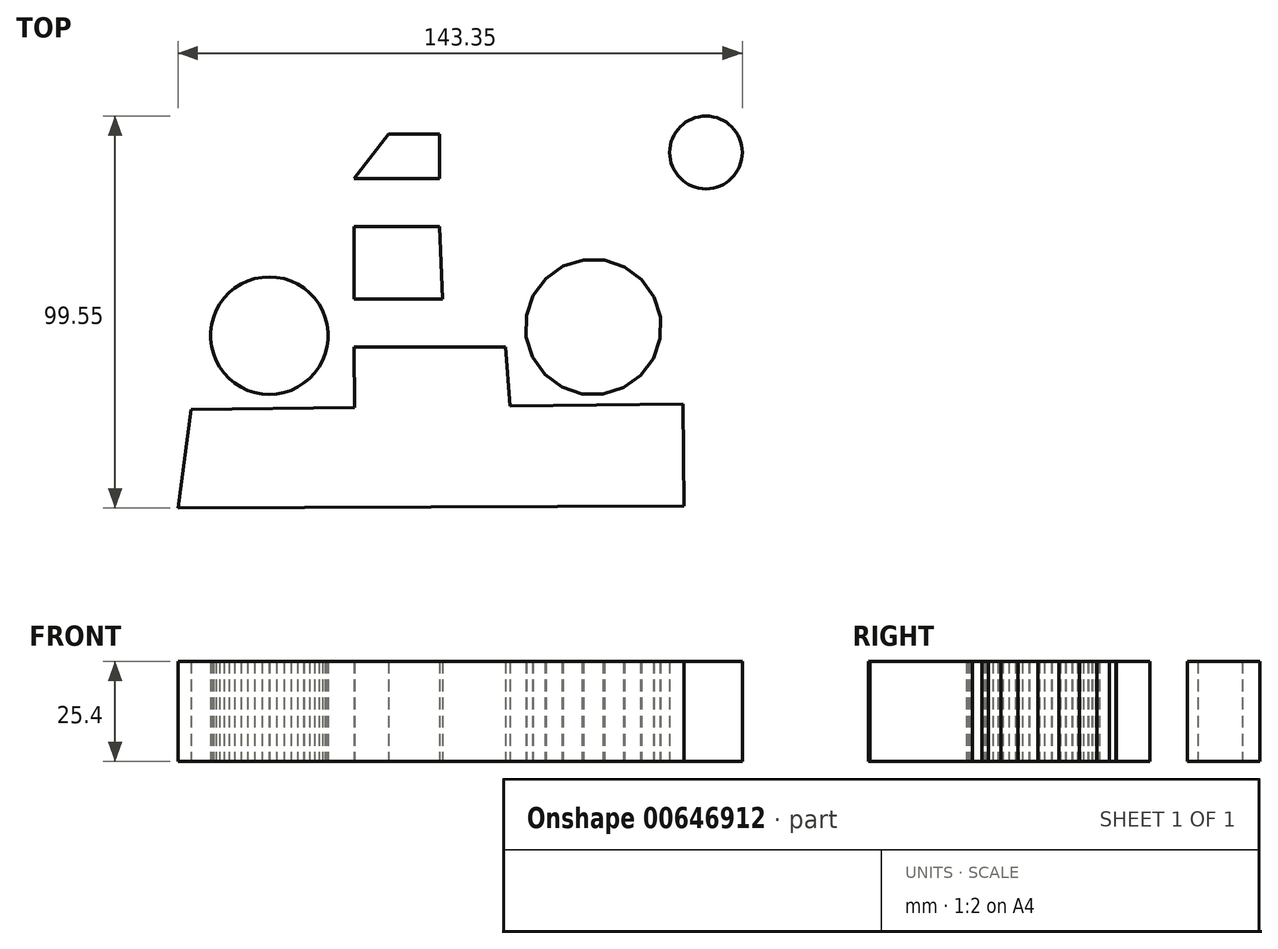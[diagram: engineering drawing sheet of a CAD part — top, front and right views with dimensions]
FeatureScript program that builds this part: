
annotation { "Feature Type Name" : "Feature", "Feature Type Description" : "" }
export const myFeature = defineFeature(function(context is Context, id is Id, definition is map)
    precondition{}
    {
        {
            var Q0;
            Q0=qCreatedBy(makeId("Top.planeOp"),FACE);
            var sketch = newSketch(context, id + "F0", { "sketchPlane" : qUnion([Q0])});
            skCircle(sketch, "E0.cCircle", {"center": v(-44.06, -3.83) * mm, "radius": 14.9 * mm, "construction": true});
            skLineSegment(sketch, "E0.0", {"start": v(-33.85, -14.73) * mm, "end": v(-35.3, -15.92) * mm});
            skLineSegment(sketch, "E0.1", {"start": v(-35.3, -15.92) * mm, "end": v(-36.88, -16.93) * mm});
            skLineSegment(sketch, "E0.2", {"start": v(-36.88, -16.93) * mm, "end": v(-38.58, -17.72) * mm});
            skLineSegment(sketch, "E0.3", {"start": v(-38.58, -17.72) * mm, "end": v(-40.37, -18.3) * mm});
            skLineSegment(sketch, "E0.4", {"start": v(-40.37, -18.3) * mm, "end": v(-42.2, -18.65) * mm});
            skLineSegment(sketch, "E0.5", {"start": v(-42.2, -18.65) * mm, "end": v(-44.08, -18.77) * mm});
            skLineSegment(sketch, "E0.6", {"start": v(-44.08, -18.77) * mm, "end": v(-45.95, -18.65) * mm});
            skLineSegment(sketch, "E0.7", {"start": v(-45.95, -18.65) * mm, "end": v(-47.8, -18.3) * mm});
            skLineSegment(sketch, "E0.8", {"start": v(-47.8, -18.3) * mm, "end": v(-49.58, -17.71) * mm});
            skLineSegment(sketch, "E0.9", {"start": v(-49.58, -17.71) * mm, "end": v(-51.27, -16.91) * mm});
            skLineSegment(sketch, "E0.10", {"start": v(-51.27, -16.91) * mm, "end": v(-52.86, -15.9) * mm});
            skLineSegment(sketch, "E0.11", {"start": v(-52.86, -15.9) * mm, "end": v(-54.3, -14.7) * mm});
            skLineSegment(sketch, "E0.12", {"start": v(-54.3, -14.7) * mm, "end": v(-55.58, -13.34) * mm});
            skLineSegment(sketch, "E0.13", {"start": v(-55.58, -13.34) * mm, "end": v(-56.68, -11.82) * mm});
            skLineSegment(sketch, "E0.14", {"start": v(-56.68, -11.82) * mm, "end": v(-57.59, -10.18) * mm});
            skLineSegment(sketch, "E0.15", {"start": v(-57.59, -10.18) * mm, "end": v(-58.27, -8.43) * mm});
            skLineSegment(sketch, "E0.16", {"start": v(-58.27, -8.43) * mm, "end": v(-58.74, -6.61) * mm});
            skLineSegment(sketch, "E0.17", {"start": v(-58.74, -6.61) * mm, "end": v(-58.97, -4.75) * mm});
            skLineSegment(sketch, "E0.18", {"start": v(-58.97, -4.75) * mm, "end": v(-58.97, -2.88) * mm});
            skLineSegment(sketch, "E0.19", {"start": v(-58.97, -2.88) * mm, "end": v(-58.73, -1.02) * mm});
            skLineSegment(sketch, "E0.20", {"start": v(-58.73, -1.02) * mm, "end": v(-58.26, 0.8) * mm});
            skLineSegment(sketch, "E0.21", {"start": v(-58.26, 0.8) * mm, "end": v(-57.57, 2.54) * mm});
            skLineSegment(sketch, "E0.22", {"start": v(-57.57, 2.54) * mm, "end": v(-56.67, 4.18) * mm});
            skLineSegment(sketch, "E0.23", {"start": v(-56.67, 4.18) * mm, "end": v(-55.56, 5.7) * mm});
            skLineSegment(sketch, "E0.24", {"start": v(-55.56, 5.7) * mm, "end": v(-54.28, 7.07) * mm});
            skLineSegment(sketch, "E0.25", {"start": v(-54.28, 7.07) * mm, "end": v(-52.83, 8.26) * mm});
            skLineSegment(sketch, "E0.26", {"start": v(-52.83, 8.26) * mm, "end": v(-51.25, 9.26) * mm});
            skLineSegment(sketch, "E0.27", {"start": v(-51.25, 9.26) * mm, "end": v(-49.55, 10.06) * mm});
            skLineSegment(sketch, "E0.28", {"start": v(-49.55, 10.06) * mm, "end": v(-47.76, 10.64) * mm});
            skLineSegment(sketch, "E0.29", {"start": v(-47.76, 10.64) * mm, "end": v(-45.92, 10.99) * mm});
            skLineSegment(sketch, "E0.30", {"start": v(-45.92, 10.99) * mm, "end": v(-44.05, 11.1) * mm});
            skLineSegment(sketch, "E0.31", {"start": v(-44.05, 11.1) * mm, "end": v(-42.18, 10.98) * mm});
            skLineSegment(sketch, "E0.32", {"start": v(-42.18, 10.98) * mm, "end": v(-40.33, 10.63) * mm});
            skLineSegment(sketch, "E0.33", {"start": v(-40.33, 10.63) * mm, "end": v(-38.55, 10.05) * mm});
            skLineSegment(sketch, "E0.34", {"start": v(-38.55, 10.05) * mm, "end": v(-36.86, 9.25) * mm});
            skLineSegment(sketch, "E0.35", {"start": v(-36.86, 9.25) * mm, "end": v(-35.27, 8.24) * mm});
            skLineSegment(sketch, "E0.36", {"start": v(-35.27, 8.24) * mm, "end": v(-33.83, 7.04) * mm});
            skLineSegment(sketch, "E0.37", {"start": v(-33.83, 7.04) * mm, "end": v(-32.55, 5.68) * mm});
            skLineSegment(sketch, "E0.38", {"start": v(-32.55, 5.68) * mm, "end": v(-31.45, 4.16) * mm});
            skLineSegment(sketch, "E0.39", {"start": v(-31.45, 4.16) * mm, "end": v(-30.54, 2.51) * mm});
            skLineSegment(sketch, "E0.40", {"start": v(-30.54, 2.51) * mm, "end": v(-29.86, 0.77) * mm});
            skLineSegment(sketch, "E0.41", {"start": v(-29.86, 0.77) * mm, "end": v(-29.4, -1.05) * mm});
            skLineSegment(sketch, "E0.42", {"start": v(-29.4, -1.05) * mm, "end": v(-29.16, -2.91) * mm});
            skLineSegment(sketch, "E0.43", {"start": v(-29.16, -2.91) * mm, "end": v(-29.16, -4.79) * mm});
            skLineSegment(sketch, "E0.44", {"start": v(-29.16, -4.79) * mm, "end": v(-29.4, -6.65) * mm});
            skLineSegment(sketch, "E0.45", {"start": v(-29.4, -6.65) * mm, "end": v(-29.87, -8.46) * mm});
            skLineSegment(sketch, "E0.46", {"start": v(-29.87, -8.46) * mm, "end": v(-30.56, -10.2) * mm});
            skLineSegment(sketch, "E0.47", {"start": v(-30.56, -10.2) * mm, "end": v(-31.46, -11.85) * mm});
            skLineSegment(sketch, "E0.48", {"start": v(-31.46, -11.85) * mm, "end": v(-32.57, -13.36) * mm});
            skLineSegment(sketch, "E0.49", {"start": v(-32.57, -13.36) * mm, "end": v(-33.85, -14.73) * mm});
            skPoint(sketch, "E0.0.midPoint", {"position": v(-34.58, -15.33) * mm});
            skCircle(sketch, "E1.cCircle", {"center": v(38.23, -1.64) * mm, "radius": 17.01 * mm, "construction": true});
            skLineSegment(sketch, "E1.0", {"start": v(50.28, -13.95) * mm, "end": v(45.88, -17.07) * mm});
            skLineSegment(sketch, "E1.1", {"start": v(45.88, -17.07) * mm, "end": v(40.74, -18.68) * mm});
            skLineSegment(sketch, "E1.2", {"start": v(40.74, -18.68) * mm, "end": v(35.35, -18.62) * mm});
            skLineSegment(sketch, "E1.3", {"start": v(35.35, -18.62) * mm, "end": v(30.25, -16.9) * mm});
            skLineSegment(sketch, "E1.4", {"start": v(30.25, -16.9) * mm, "end": v(25.92, -13.7) * mm});
            skLineSegment(sketch, "E1.5", {"start": v(25.92, -13.7) * mm, "end": v(22.8, -9.3) * mm});
            skLineSegment(sketch, "E1.6", {"start": v(22.8, -9.3) * mm, "end": v(21.19, -4.16) * mm});
            skLineSegment(sketch, "E1.7", {"start": v(21.19, -4.16) * mm, "end": v(21.24, 1.23) * mm});
            skLineSegment(sketch, "E1.8", {"start": v(21.24, 1.23) * mm, "end": v(22.96, 6.34) * mm});
            skLineSegment(sketch, "E1.9", {"start": v(22.96, 6.34) * mm, "end": v(26.18, 10.66) * mm});
            skLineSegment(sketch, "E1.10", {"start": v(26.18, 10.66) * mm, "end": v(30.57, 13.79) * mm});
            skLineSegment(sketch, "E1.11", {"start": v(30.57, 13.79) * mm, "end": v(35.71, 15.4) * mm});
            skLineSegment(sketch, "E1.12", {"start": v(35.71, 15.4) * mm, "end": v(41.1, 15.34) * mm});
            skLineSegment(sketch, "E1.13", {"start": v(41.1, 15.34) * mm, "end": v(46.2, 13.62) * mm});
            skLineSegment(sketch, "E1.14", {"start": v(46.2, 13.62) * mm, "end": v(50.53, 10.4) * mm});
            skLineSegment(sketch, "E1.15", {"start": v(50.53, 10.4) * mm, "end": v(53.65, 6.01) * mm});
            skLineSegment(sketch, "E1.16", {"start": v(53.65, 6.01) * mm, "end": v(55.26, 0.87) * mm});
            skLineSegment(sketch, "E1.17", {"start": v(55.26, 0.87) * mm, "end": v(55.2, -4.52) * mm});
            skLineSegment(sketch, "E1.18", {"start": v(55.2, -4.52) * mm, "end": v(53.49, -9.62) * mm});
            skLineSegment(sketch, "E1.19", {"start": v(53.49, -9.62) * mm, "end": v(50.28, -13.95) * mm});
            skPoint(sketch, "E1.0.midPoint", {"position": v(48.08, -15.5) * mm});
            skSolve(sketch);
        }
        {
            var Q0;
            Q0=makeQuery(id+"F0.imprint","IMPRINT",FACE,{"disambiguationData":[TD([[makeQuery(id+"F0.imprint","IMPRINT",EDGE,{"derivedFrom":sQuery(id+"F0.wireOp",EDGE,"E0.0")}),-1.0]])]});
            var Q1;
            Q1=makeQuery(id+"F0.imprint","IMPRINT",FACE,{"disambiguationData":[TD([[makeQuery(id+"F0.imprint","IMPRINT",EDGE,{"derivedFrom":sQuery(id+"F0.wireOp",EDGE,"E1.0")}),-1.0]])]});
            extrude(context, id + "F1", {"entities" : qUnion([Q0, Q1]), "depth" : 25.4 * mm, "offsetDistance" : 25.4 * mm});
        }
        {
            var Q0;
            Q0=qCreatedBy(makeId("Top.planeOp"),FACE);
            var sketch = newSketch(context, id + "F2", { "sketchPlane" : qUnion([Q0])});
            skLineSegment(sketch, "E2", {"start": v(-35.67, 32.3) * mm, "end": v(-55.2, 32.3) * mm});
            skLineSegment(sketch, "E3", {"start": v(-55.2, 32.3) * mm, "end": v(-55.2, 18.06) * mm});
            skLineSegment(sketch, "E4", {"start": v(-55.2, 18.06) * mm, "end": v(-44.06, 18.06) * mm});
            skLineSegment(sketch, "E5", {"start": v(-44.06, 18.06) * mm, "end": v(-33.48, 6.75) * mm});
            skLineSegment(sketch, "E6", {"start": v(-35.67, 32.3) * mm, "end": v(-22.53, 52.55) * mm});
            skLineSegment(sketch, "E7", {"start": v(-22.53, 52.55) * mm, "end": v(57.75, 52.55) * mm});
            skLineSegment(sketch, "E8", {"start": v(57.75, 52.55) * mm, "end": v(57.75, 23.9) * mm});
            skLineSegment(sketch, "E9", {"start": v(57.75, 23.9) * mm, "end": v(29.29, 13.32) * mm});
            skLineSegment(sketch, "E10", {"start": v(-28.56, -4.38) * mm, "end": v(20.9, -4.38) * mm});
            skLineSegment(sketch, "E11", {"start": v(21.62, 3.47) * mm, "end": v(-29.83, 1.46) * mm});
            skLineSegment(sketch, "E12", {"start": v(-22.53, 36.13) * mm, "end": v(-0.82, 36.13) * mm});
            skLineSegment(sketch, "E13", {"start": v(-0.82, 36.13) * mm, "end": v(-0.82, 47.44) * mm});
            skLineSegment(sketch, "E14", {"start": v(-0.82, 47.44) * mm, "end": v(-13.78, 47.44) * mm});
            skLineSegment(sketch, "E15", {"start": v(-13.78, 47.44) * mm, "end": v(-22.53, 36.13) * mm});
            skLineSegment(sketch, "E16", {"start": v(-22.53, 23.9) * mm, "end": v(-0.82, 23.9) * mm});
            skLineSegment(sketch, "E17", {"start": v(-0.82, 23.9) * mm, "end": v(-0.1, 5.49) * mm});
            skLineSegment(sketch, "E18", {"start": v(-0.1, 5.49) * mm, "end": v(-22.53, 5.49) * mm});
            skLineSegment(sketch, "E19", {"start": v(-22.53, 5.49) * mm, "end": v(-22.53, 23.9) * mm});
            skSolve(sketch);
        }
        {
            var Q0;
            Q0=qCreatedBy(makeId("Top.planeOp"),FACE);
            var sketch = newSketch(context, id + "F3", { "sketchPlane" : qUnion([Q0])});
            skCircle(sketch, "E20", {"center": v(66.87, 42.7) * mm, "radius": 9.24 * mm});
            skSolve(sketch);
        }
        {
            var Q0;
            Q0=makeQuery(id+"F3.imprint","IMPRINT",FACE,{"disambiguationData":[TD([[makeQuery(id+"F3.imprint","IMPRINT",EDGE,{"derivedFrom":sQuery(id+"F3.wireOp",EDGE,"E20")}),1.0]])]});
            var Q1;
            Q1=makeQuery(id+"F2.imprint","IMPRINT",FACE,{"disambiguationData":[TD([[makeQuery(id+"F2.imprint","IMPRINT",EDGE,{"derivedFrom":sQuery(id+"F2.wireOp",EDGE,"E12")}),1.0]])]});
            var Q2;
            Q2=makeQuery(id+"F2.imprint","IMPRINT",FACE,{"disambiguationData":[TD([[makeQuery(id+"F2.imprint","IMPRINT",EDGE,{"derivedFrom":sQuery(id+"F2.wireOp",EDGE,"E16")}),-1.0]])]});
            extrude(context, id + "F4", {"entities" : qUnion([Q0, Q1, Q2]), "depth" : 25.4 * mm, "offsetDistance" : 25.4 * mm});
        }
        {
            var Q0;
            Q0=qCreatedBy(makeId("Top.planeOp"),FACE);
            var sketch = newSketch(context, id + "F5", { "sketchPlane" : qUnion([Q0])});
            skLineSegment(sketch, "E21", {"start": v(-50.45, 19.89) * mm, "end": v(-33.3, 7.12) * mm});
            skLineSegment(sketch, "E22", {"start": v(-50.45, 19.89) * mm, "end": v(-50.45, 31.57) * mm});
            skLineSegment(sketch, "E23", {"start": v(-50.27, 31.57) * mm, "end": v(-40.05, 31.57) * mm});
            skLineSegment(sketch, "E24", {"start": v(-40.05, 31.57) * mm, "end": v(-17.06, 62.45) * mm});
            skLineSegment(sketch, "E25", {"start": v(-17.06, 62.45) * mm, "end": v(55.92, 62.45) * mm});
            skLineSegment(sketch, "E26", {"start": v(55.92, 62.45) * mm, "end": v(53.92, 7.12) * mm});
            skLineSegment(sketch, "E27", {"start": v(-30.02, -6.75) * mm, "end": v(21.26, -6.75) * mm});
            skLineSegment(sketch, "E28", {"start": v(21.07, 1.46) * mm, "end": v(-29.65, 1.46) * mm});
            skLineSegment(sketch, "E29", {"start": v(40.6, 46.16) * mm, "end": v(25.09, 45.98) * mm});
            skLineSegment(sketch, "E30", {"start": v(25.09, 45.98) * mm, "end": v(25.22, 34.68) * mm});
            skLineSegment(sketch, "E31", {"start": v(25.22, 34.68) * mm, "end": v(41.51, 34.87) * mm});
            skLineSegment(sketch, "E32", {"start": v(41.51, 35.22) * mm, "end": v(40.6, 46.35) * mm});
            skLineSegment(sketch, "E33", {"start": v(27.46, 34.7) * mm, "end": v(27.63, 19.89) * mm});
            skLineSegment(sketch, "E34", {"start": v(41.51, 34.87) * mm, "end": v(27.63, 19.89) * mm});
            skLineSegment(sketch, "E35", {"start": v(27.63, 19.89) * mm, "end": v(-0.46, 5.66) * mm});
            skLineSegment(sketch, "E36", {"start": v(25.09, 45.98) * mm, "end": v(-0.46, 37.22) * mm});
            skLineSegment(sketch, "E37", {"start": v(-16.88, 62.77) * mm, "end": v(-17.06, 67.88) * mm});
            skLineSegment(sketch, "E38", {"start": v(-17.06, 67.88) * mm, "end": v(56.29, 67.88) * mm});
            skLineSegment(sketch, "E39", {"start": v(56.29, 67.88) * mm, "end": v(55.92, 62.77) * mm});
            skLineSegment(sketch, "E40", {"start": v(56.29, 67.88) * mm, "end": v(56.29, 71.7) * mm});
            skLineSegment(sketch, "E41", {"start": v(53.74, 68.06) * mm, "end": v(53.55, 71.34) * mm});
            skLineSegment(sketch, "E42", {"start": v(50.63, 67.7) * mm, "end": v(51, 70.61) * mm});
            skLineSegment(sketch, "E43", {"start": v(48.44, 67.51) * mm, "end": v(47.71, 71.34) * mm});
            skLineSegment(sketch, "E44", {"start": v(42.6, 66.96) * mm, "end": v(43.33, 70.98) * mm});
            skLineSegment(sketch, "E45", {"start": v(39.87, 67.15) * mm, "end": v(40.6, 70.98) * mm});
            skLineSegment(sketch, "E46", {"start": v(36.77, 66.96) * mm, "end": v(37.13, 70.98) * mm});
            skLineSegment(sketch, "E47", {"start": v(31.84, 66.6) * mm, "end": v(32.2, 70.8) * mm});
            skLineSegment(sketch, "E48", {"start": v(44.98, 68.06) * mm, "end": v(45.34, 71.34) * mm});
            skLineSegment(sketch, "E49", {"start": v(29.29, 67.51) * mm, "end": v(30.2, 70.25) * mm});
            skLineSegment(sketch, "E50", {"start": v(30.2, 70.25) * mm, "end": v(27.1, 67.7) * mm});
            skLineSegment(sketch, "E51", {"start": v(27.1, 67.7) * mm, "end": v(25.27, 70.98) * mm});
            skLineSegment(sketch, "E52", {"start": v(25.27, 70.98) * mm, "end": v(22.72, 68.42) * mm});
            skLineSegment(sketch, "E53", {"start": v(22.72, 68.42) * mm, "end": v(19.7, 70.67) * mm});
            skLineSegment(sketch, "E54", {"start": v(19.7, 70.67) * mm, "end": v(16.33, 67.33) * mm});
            skLineSegment(sketch, "E55", {"start": v(16.33, 67.33) * mm, "end": v(13.24, 70.45) * mm});
            skLineSegment(sketch, "E56", {"start": v(13.24, 70.45) * mm, "end": v(12.86, 68.42) * mm});
            skLineSegment(sketch, "E57", {"start": v(12.86, 68.42) * mm, "end": v(11.04, 69.7) * mm});
            skLineSegment(sketch, "E58", {"start": v(11.04, 69.7) * mm, "end": v(10.13, 70.61) * mm});
            skLineSegment(sketch, "E59", {"start": v(10.13, 70.61) * mm, "end": v(6.11, 69.88) * mm});
            skLineSegment(sketch, "E60", {"start": v(4.65, 70.25) * mm, "end": v(2.46, 70.43) * mm});
            skLineSegment(sketch, "E61", {"start": v(2.46, 70.43) * mm, "end": v(-0.46, 68.6) * mm});
            skLineSegment(sketch, "E62", {"start": v(-0.46, 68.6) * mm, "end": v(-13.96, 68.79) * mm});
            skLineSegment(sketch, "E63", {"start": v(-16.33, 68.79) * mm, "end": v(-17.06, 67.88) * mm});
            skLineSegment(sketch, "E64", {"start": v(-16.33, 68.79) * mm, "end": v(-13.96, 68.79) * mm});
            skLineSegment(sketch, "E65", {"start": v(-22.53, -6.75) * mm, "end": v(-22.05, -47.6) * mm});
            skLineSegment(sketch, "E66", {"start": v(-22.05, -47.6) * mm, "end": v(18.87, -47.13) * mm});
            skLineSegment(sketch, "E67", {"start": v(18.87, -47.13) * mm, "end": v(15.97, -6.75) * mm});
            skLineSegment(sketch, "E68", {"start": v(-63.95, -22.63) * mm, "end": v(61.04, -21.15) * mm});
            skLineSegment(sketch, "E69", {"start": v(61.04, -21.15) * mm, "end": v(61.35, -47.13) * mm});
            skLineSegment(sketch, "E70", {"start": v(61.35, -47.13) * mm, "end": v(-67.24, -47.6) * mm});
            skLineSegment(sketch, "E71", {"start": v(-67.24, -47.6) * mm, "end": v(-63.95, -22.63) * mm});
            skSolve(sketch);
        }
        {
            var Q0;
            {var subQ5=sQuery(id+"F5.wireOp",EDGE,"E71");Q0=makeQuery(id+"F5.imprint","IMPRINT",FACE,{"disambiguationData":[TD([[makeQuery(id+"F5.imprint","IMPRINT",EDGE,{"derivedFrom":subQ5}),-1.0]])]});}
            var Q1;
            {var subQ0=sQuery(id+"F5.wireOp",EDGE,"E68");var subQ1=sQuery(id+"F5.wireOp",EDGE,"E65");var subQ2=makeQuery(id+"F5.imprint","INTERSECT",VERTEX,{"derivedFrom":[subQ1,subQ0]});Q1=makeQuery(id+"F5.imprint","IMPRINT",FACE,{"disambiguationData":[TD([[makeQuery(id+"F5.imprint","IMPRINT",EDGE,{"disambiguationData":[TD([[subQ2,-1.0]])],"derivedFrom":subQ1}),1.0]])]});}
            var Q2;
            {var subQ0=sQuery(id+"F5.wireOp",EDGE,"E65");var subQ1=sQuery(id+"F5.wireOp",EDGE,"E27");var subQ2=makeQuery(id+"F5.imprint","INTERSECT",VERTEX,{"derivedFrom":[subQ1,subQ0]});Q2=makeQuery(id+"F5.imprint","IMPRINT",FACE,{"disambiguationData":[TD([[makeQuery(id+"F5.imprint","IMPRINT",EDGE,{"disambiguationData":[TD([[subQ2,-1.0]])],"derivedFrom":subQ1}),-1.0]])]});}
            var Q3;
            {var subQ0=sQuery(id+"F5.wireOp",EDGE,"E69");Q3=makeQuery(id+"F5.imprint","IMPRINT",FACE,{"disambiguationData":[TD([[makeQuery(id+"F5.imprint","IMPRINT",EDGE,{"derivedFrom":subQ0}),-1.0]])]});}
            extrude(context, id + "F6", {"entities" : qUnion([Q0, Q1, Q2, Q3]), "depth" : 25.4 * mm, "offsetDistance" : 25.4 * mm});
        }
    });
